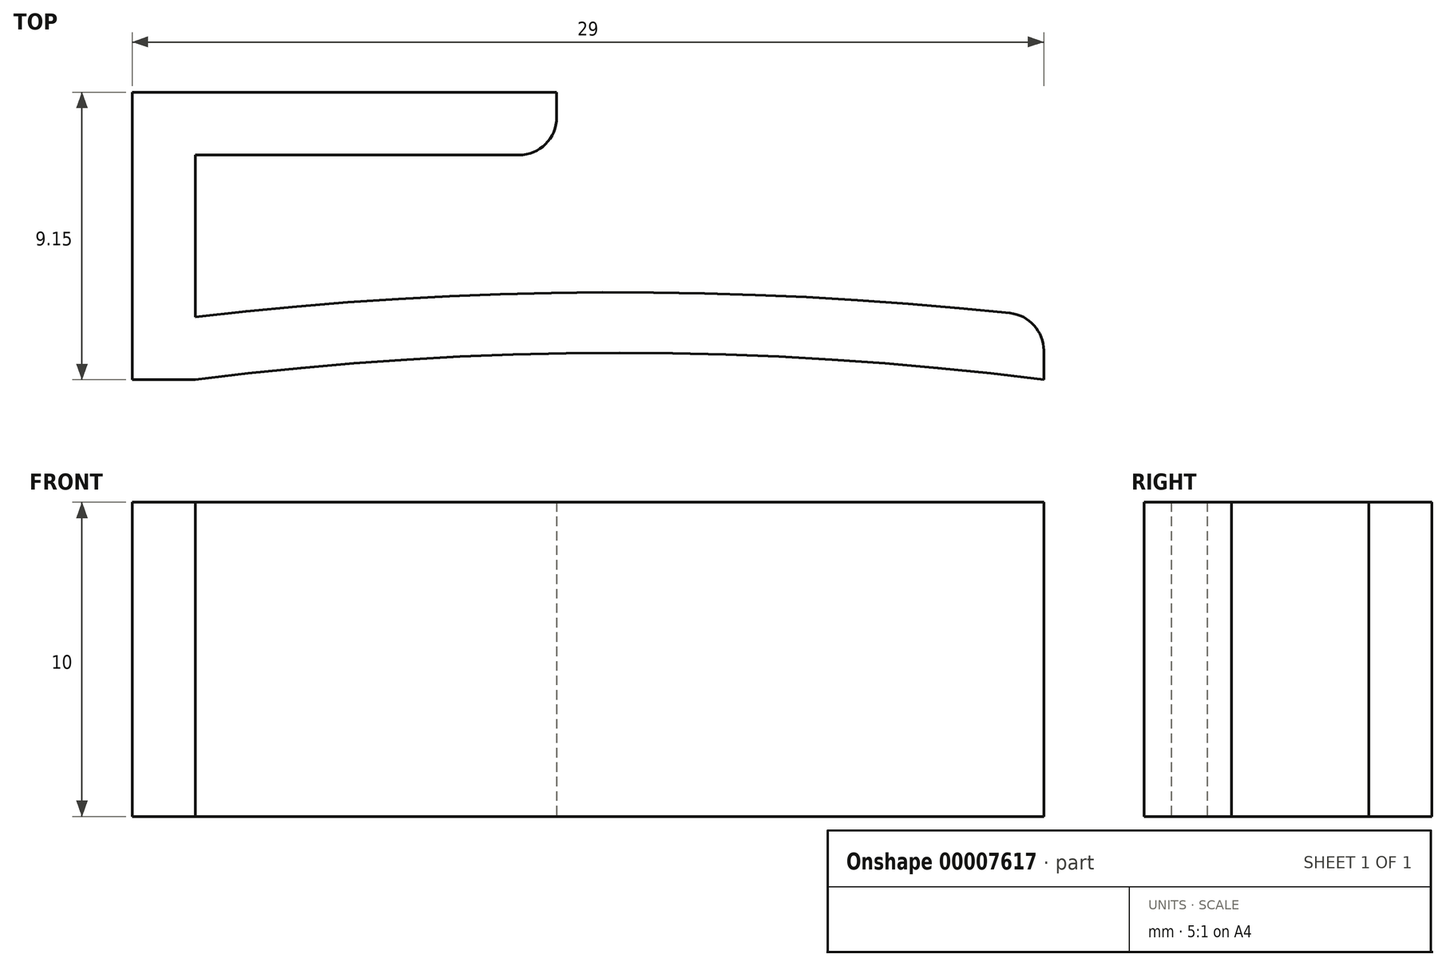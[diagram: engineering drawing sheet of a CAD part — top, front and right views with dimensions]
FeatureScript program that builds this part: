
annotation { "Feature Type Name" : "Feature", "Feature Type Description" : "" }
export const myFeature = defineFeature(function(context is Context, id is Id, definition is map)
    precondition{}
    {
        {
            var Q0;
            Q0=qCreatedBy(makeId("Top.planeOp"),FACE);
            var sketch = newSketch(context, id + "F0", { "sketchPlane" : qUnion([Q0])});
            skLineSegment(sketch, "E0", {"start": v(0, 3.77) * mm, "end": v(0, 5.77) * mm});
            skLineSegment(sketch, "E1", {"start": v(0, 5.77) * mm, "end": v(-13.5, 5.77) * mm});
            skLineSegment(sketch, "E2", {"start": v(-13.5, 5.77) * mm, "end": v(-13.5, -3.38) * mm});
            skLineSegment(sketch, "E3", {"start": v(-11.5, -1.38) * mm, "end": v(-11.5, 3.77) * mm});
            skLineSegment(sketch, "E4", {"start": v(-11.5, 3.77) * mm, "end": v(0, 3.77) * mm});
            skLineSegment(sketch, "E5", {"start": v(-13.5, -3.38) * mm, "end": v(-11.5, -3.38) * mm});
            skArc(sketch, "E6", {"start": v(15.5, -1.38) * mm, "mid": v(2, -0.6) * mm, "end": v(-11.5, -1.38) * mm});
            skArc(sketch, "E7", {"start": v(15.5, -3.38) * mm, "mid": v(2, -2.53) * mm, "end": v(-11.5, -3.38) * mm});
            skLineSegment(sketch, "E8", {"start": v(15.5, -1.38) * mm, "end": v(15.5, -3.38) * mm});
            skSolve(sketch);
        }
        {
            var Q0;
            Q0 = qSketchRegion(id + "F0", true);
            extrude(context, id + "F1", {"entities" : qUnion([Q0]), "depth" : 10 * mm});
        }
        {
            var Q0;
            Q0=makeQuery(id+"F1.opExtrude","SWEPT_EDGE",EDGE,{"disambiguationData":[OSD([sQuery(id+"F0.wireOp",EDGE,"E0"),sQuery(id+"F0.wireOp",EDGE,"E4")])]});
            var Q1;
            Q1=makeQuery(id+"F1.opExtrude","SWEPT_EDGE",EDGE,{"disambiguationData":[OSD([sQuery(id+"F0.wireOp",EDGE,"136c5863-876e-4df1-b1e1-ec6da6344faf"),sQuery(id+"F0.wireOp",EDGE,"8ada92fe-2a60-449d-b6a4-9f05347f9e42")])]});
            var Q2;
            Q2=makeQuery(id+"F1.opExtrude","SWEPT_EDGE",EDGE,{"disambiguationData":[OSD([sQuery(id+"F0.wireOp",EDGE,"E6"),sQuery(id+"F0.wireOp",EDGE,"E8")])]});
            fillet(context, id + "F2", {"entities" : qUnion([Q0, Q1, Q2]), "radius" : 1.2 * mm, "tangentPropagation" : true, "allowEdgeOverflow" : false});
        }
    });
